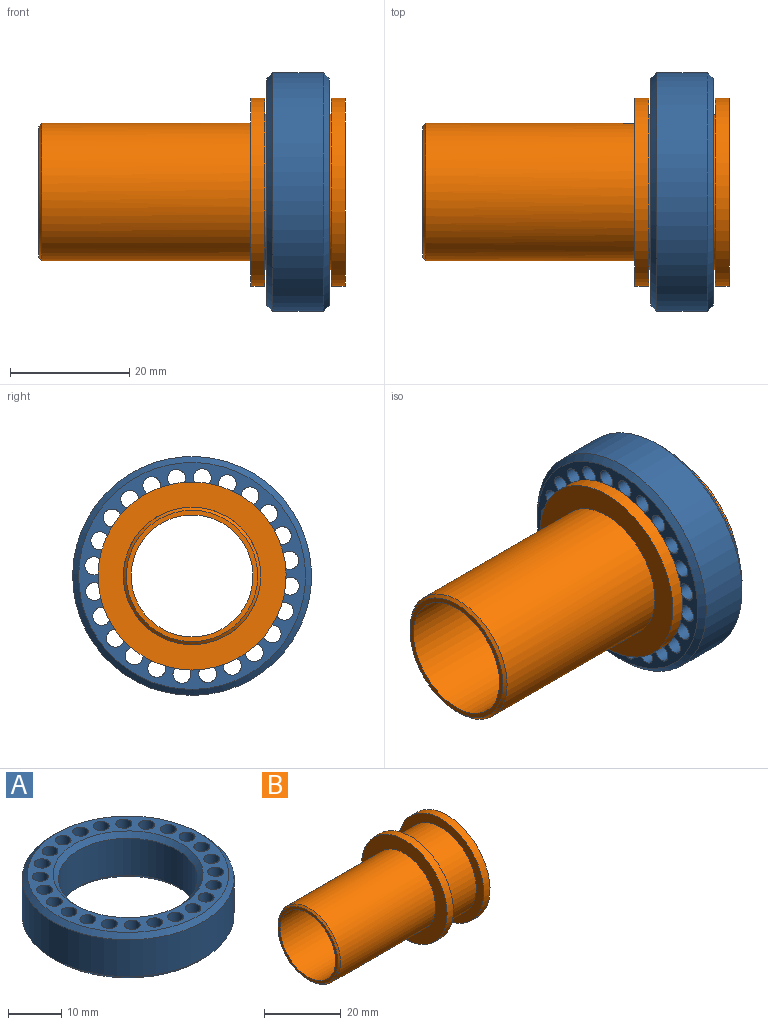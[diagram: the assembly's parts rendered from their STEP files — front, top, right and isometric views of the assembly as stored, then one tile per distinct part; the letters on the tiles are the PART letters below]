
ASSEMBLY  parts=2 mates=1
PART A: 32 faces, bbox 40x40x10.5 mm
  f0: cylinder r=13.15mm len=26.3mm, axis (0,0,-1), area 702.3mm2, adj f6,f7
  f1: cylinder r=20mm len=40mm, axis (0,0,-1), area 1068.1mm2, adj f4,f5
  f2: plane 38x38mm, normal (0,0,1), area 335.5mm2, adj f4,f7,f8,f9,f10,f11,f12,f13
  f3: plane 38x38mm, normal (0,0,-1), area 335.5mm2, adj f5,f6,f8,f9,f10,f11,f12,f13
  f4: cone r=19mm half-angle=45deg, axis (0,0,-1), area 173.3mm2, adj f1,f2
  f5: cone r=20mm half-angle=45deg, axis (0,0,1), area 173.3mm2, adj f1,f3
  f6: cone r=14.15mm half-angle=45deg, axis (0,0,-1), area 121.3mm2, adj f0,f3
  f7: cone r=13.15mm half-angle=45deg, axis (0,0,1), area 121.3mm2, adj f0,f2
  f8: cylinder r=1.5mm len=10.5mm, axis (0,0,1), area 99mm2, adj f2,f3
  f9: cylinder r=1.5mm len=10.5mm, axis (0,0,1), area 99mm2, adj f2,f3
  f10: cylinder r=1.5mm len=10.5mm, axis (0,0,1), area 99mm2, adj f2,f3
  f11: cylinder r=1.5mm len=10.5mm, axis (0,0,1), area 99mm2, adj f2,f3
  f12: cylinder r=1.5mm len=10.5mm, axis (0,0,1), area 99mm2, adj f2,f3
  f13: cylinder r=1.5mm len=10.5mm, axis (0,0,1), area 99mm2, adj f2,f3
  f14: cylinder r=1.5mm len=10.5mm, axis (0,0,1), area 99mm2, adj f2,f3
  f15: cylinder r=1.5mm len=10.5mm, axis (0,0,1), area 99mm2, adj f2,f3
  f16: cylinder r=1.5mm len=10.5mm, axis (0,0,1), area 99mm2, adj f2,f3
  f17: cylinder r=1.5mm len=10.5mm, axis (0,0,1), area 99mm2, adj f2,f3
  f18: cylinder r=1.5mm len=10.5mm, axis (0,0,1), area 99mm2, adj f2,f3
  f19: cylinder r=1.5mm len=10.5mm, axis (0,0,1), area 99mm2, adj f2,f3
  f20: cylinder r=1.5mm len=10.5mm, axis (0,0,1), area 99mm2, adj f2,f3
  f21: cylinder r=1.5mm len=10.5mm, axis (0,0,1), area 99mm2, adj f2,f3
  f22: cylinder r=1.5mm len=10.5mm, axis (0,0,1), area 99mm2, adj f2,f3
  f23: cylinder r=1.5mm len=10.5mm, axis (0,0,1), area 99mm2, adj f2,f3
  f24: cylinder r=1.5mm len=10.5mm, axis (0,0,1), area 99mm2, adj f2,f3
  f25: cylinder r=1.5mm len=10.5mm, axis (0,0,1), area 99mm2, adj f2,f3
  f26: cylinder r=1.5mm len=10.5mm, axis (0,0,1), area 99mm2, adj f2,f3
  f27: cylinder r=1.5mm len=10.5mm, axis (0,0,1), area 99mm2, adj f2,f3
  f28: cylinder r=1.5mm len=10.5mm, axis (0,0,1), area 99mm2, adj f2,f3
  f29: cylinder r=1.5mm len=10.5mm, axis (0,0,1), area 99mm2, adj f2,f3
  f30: cylinder r=1.5mm len=10.5mm, axis (0,0,1), area 99mm2, adj f2,f3
  f31: cylinder r=1.5mm len=10.5mm, axis (0,0,1), area 99mm2, adj f2,f3
PART B: 12 faces, bbox 51.3x31.5x31.5 mm
  f0: cylinder r=11.5mm len=35mm, axis (1,0,0), area 2529mm2, adj f9,f11
  f1: plane 22x22mm, normal (-1,0,0), area 53.3mm2, adj f2,f11
  f2: cylinder r=10.2mm len=50.8mm, axis (1,0,0), area 3255.7mm2, adj f1,f10
  f3: plane 31.5x31.5mm, normal (1,0,0), area 419.6mm2, adj f4,f10
  f4: cylinder r=15.75mm len=31.5mm, axis (1,0,0), area 227.6mm2, adj f3,f5
  f5: plane 31.5x31.5mm, normal (-1,0,0), area 248.4mm2, adj f4,f6
  f6: cylinder r=13mm len=26mm, axis (1,0,0), area 914.8mm2, adj f5,f7
  f7: plane 31.5x31.5mm, normal (1,0,0), area 248.4mm2, adj f6,f8
  f8: cylinder r=15.75mm len=31.5mm, axis (1,0,0), area 227.6mm2, adj f7,f9
  f9: plane 31.5x31.5mm, normal (-1,0,0), area 363.8mm2, adj f0,f8
  f10: cone r=10.2mm half-angle=45deg, axis (1,0,0), area 46.4mm2, adj f2,f3
  f11: cone r=11.5mm half-angle=45deg, axis (1,0,0), area 50mm2, adj f0,f1
PLACE A rot(axis=(0.69,-0.23,-0.69),154.5deg) t=(66.61,23.88,-6.72)mm
PLACE B t=(69.26,23.88,-6.72)mm fixed
MATE revolute A.f0 <-> B.f0  axis (1,0,0) through (61.36,23.88,-6.72)mm
